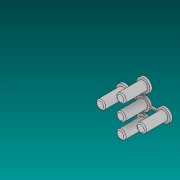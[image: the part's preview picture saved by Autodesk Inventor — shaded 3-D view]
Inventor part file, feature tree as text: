
AUTODESK INVENTOR PART (.ipt)
format: ipt  version: 2019 (Build 230136000, 136)  size: 668,160 bytes
history: native  units: mm
features: other x5, delete_face x5, sketch x4, extrude x3, fillet x2, boolean_combine x2
ambient origin geometry x8: Origin, YZ Plane, XZ Plane, XY Plane, X Axis, Y Axis, Z Axis, Center Point
bodies: Solid2 (feature_tree), Solid3 (feature_tree), Solid4 (feature_tree), Solid5 (feature_tree), Solid6 (feature_tree), Solid142 (feature_tree), Solid143 (feature_tree), Solid144 (feature_tree)
feature tree (21):
  other  "4301x60507x6_11:1"
  extrude  "Extrusion2"  Depth=4.0mm
  delete_face  "Delete Face2"
  delete_face  "Delete Face3"
  delete_face  "Delete Face4"
  delete_face  "Delete Face5"
  delete_face  "Delete Face6"
  extrude  "Extrusion3"  Depth=4.0mm
  fillet  "Fillet1"  Radius=4.0mm
  boolean_combine  "Combine1"
  extrude  "Extrusion4"  Depth=1.0mm
  sketch  "Sketch11"  dims[d22=1.0mm d23=1.0mm d32=1.0mm d33=0.0mm d34=4.0mm d35=4.0mm d36=4.0mm d37=4.0mm d38=4.0mm d39=10.0mm d40=0.0mm d41=0.5mm d42=4.0mm d43=4.0mm d44=4.0mm d45=4.0mm d46=4.0mm d47=2.0mm d48=0.0mm d49=0.5mm]
  boolean_combine  "Combine2"
  fillet  "Fillet2"  Radius=1.0mm
  sketch  "Sketch8"  dims[d14=4.0mm d15=4.0mm]
  sketch  "Sketch9"  dims[d16=4.0mm d17=4.0mm d18=4.0mm]
  sketch  "Sketch10"  dims[d19=1.0mm d20=1.0mm d21=1.0mm]
  other  "4301x60507x6_3:1"
  other  "4301x60507x6_5:1"
  other  "4301x60507x6_7:1"
  other  "4301x60507x6_9:1"
